# Revit family: PRD_FrankeWS_TltBrshHldrs_CUBUSToiletBrushHolder_CUBX005HP
name_source: partatom
category: Specialty Equipment
revit_build: Autodesk Revit 2018 (Build: 20190510_1515(x64)
units: mm (PartAtom-declared; Revit-internal decimal feet)

## family parameters
Cut with Voids When Loaded = No
Host = Face
OmniClass Number = 23.40.20.21
OmniClass Title = Toilet and Bath Specialties
Part Type = Normal
Room Calculation Point = No
Round Connector Dimension = Use Diameter
Shared = No

## types (1)
- CUBX005HP
    AssetType = Fixed
    BIMObjectName = PRD_AR_ToiletBrushHolders_CUBUSToiletBrushHolder_CUBX005HP
    BrushColour = White
    BrushMaterial = PRD_AR_ToiletBrush
    Category = Pr_40_20_76_86, Toilet brush holders
    CupMaterial = PRD_AR_FrostedGlass
    Default Elevation = 100 mm  [stored 0.328084 ft]
    Description = Toilet brush holder for wall mounting, 304 stainless steel handle with nylon brush, square glass cup, square cover with drilled hole on bottom for fixation, inclusive stainless steel screws and dowels.
    DurationUnit = year
    Features = stainless steel, surface high polished
    Finish = high polished
    GrossWeight = 1.23 kg
    HandleMaterial = PRD_AR_StainlessSteel_HighPolished
    HolderMaterial = PRD_AR_StainlessSteel_HighPolished
    IfcExportAs = IfcFurnitureType
    IfcExportType = USERDEFINED
    IntegralAccessories = incl. stainless steel screws and dowels
    IsBuiltIn = TRUE
    MainColor = stainless steel
    Manufacturer = KWC Group AG
    ManufacturerName = KWC Group AG
    ManufacturerURL = www.kwc.com
    Material = stainless steel
    MaterialCode = 1.4301
    Model = CUBX005HP
    ModelNumber = 2000106353
    ModelReference = CUBX005HP
    NBSDescription = Toilet brush holders
    NBSReference = 45-35-72/364
    Name = Toilet Brush Holder CUBX005HP
    NetWeight = 0.98 kg
    NominalDepth = 135 mm  [stored 0.442913 ft]
    NominalHeight = 340 mm  [stored 1.11549 ft]
    NominalWidth = 147 mm  [stored 0.482283 ft]
    ProductInformation = https://pim.kwc.com
    Size = 147 x 340 x 135 mm
    Style = Brush holder
    TypeOfBrush = Nylon
    TypeOfFixing = Screw
    TypeOfMounting = Wall mounting
    URL = www.kwc.com
    Uniclass2015Code = Pr_40_20_76_86
    Uniclass2015Title = Toilet brush holders
    Uniclass2015Version = Products v1.17
    Version = 1
    WarrantyDurationUnit = year

note: [stored X ft] marks values corroborated as IEEE doubles in the binary element streams (Revit-internal decimal feet)

## geometry (parser evidence)
native form markers: Sweep x2
no freeform markers — native parametric forms only
